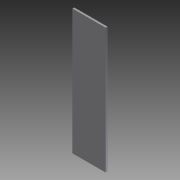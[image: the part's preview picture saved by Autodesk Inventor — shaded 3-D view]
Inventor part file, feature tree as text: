
AUTODESK INVENTOR PART (.ipt)
format: ipt  version: 2011 (Build 150239000, 239)  size: 110,592 bytes
history: native  units: in
note: dims shown in document units (in); Inventor stores cm internally (conversion verified against a paired STEP export)
features: extrude x7, sketch x7
ambient origin geometry x8: Origin, YZ Plane, XZ Plane, XY Plane, X Axis, Y Axis, Z Axis, Center Point
bodies: Solid1 (feature_tree)
feature tree (14):
  extrude  "Extrusion1"  Depth=12.0in
  extrude  "Extrusion2"  Depth=0.5in TaperAngle=0.0deg
  extrude  "Extrusion3"  Depth=10.0in
  extrude  "Extrusion4"  Depth=5.0in TaperAngle=0.0deg
  extrude  "Extrusion5"  Depth=1.0in TaperAngle=0.0deg
  extrude  "Extrusion6"  Depth=0.25in TaperAngle=0.0deg
  extrude  "Extrusion7"  [1 undecoded]
  sketch  "Sketch1"  dims[d0=5.5in d1=12.0in]
  sketch  "Sketch2"  dims[d2=0.25in d3=0.0in d4=0.5in d5=0.0in]
  sketch  "Sketch3"  dims[d6=1.5in d7=0.0in d9=10.0in]
  sketch  "Sketch5"  dims[d10=0.25in d11=0.0in d12=5.0in d13=0.0in]
  sketch  "Sketch6"  dims[d14=0.25in d15=1.0in d16=0.0in]
  sketch  "Sketch7"  dims[d17=0.25in d18=0.25in d19=0.0in]
  sketch  "Sketch8"
note: 1 required parameter value undecoded (feature->parameter linkage not recoverable at this tier; creation-order binding heuristic only, values carry confidence <= 0.55)
